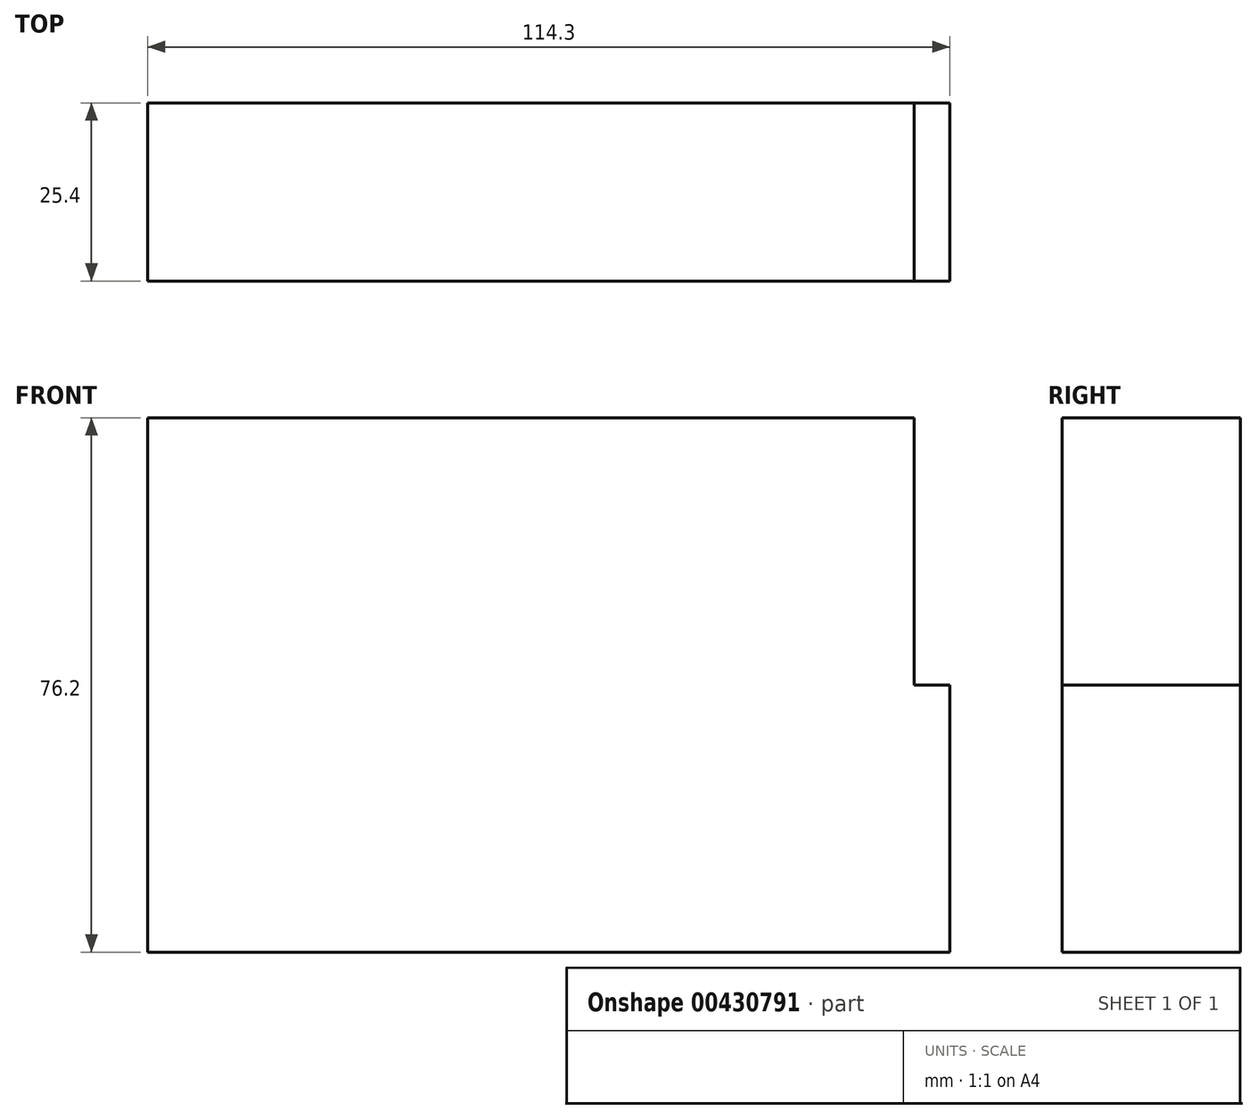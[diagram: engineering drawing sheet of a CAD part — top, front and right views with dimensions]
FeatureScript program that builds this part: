
annotation { "Feature Type Name" : "Feature", "Feature Type Description" : "" }
export const myFeature = defineFeature(function(context is Context, id is Id, definition is map)
    precondition{}
    {
        {
            var Q0;
            Q0=qCreatedBy(makeId("Front.planeOp"),FACE);
            var sketch = newSketch(context, id + "F0", { "sketchPlane" : qUnion([Q0])});
            skLineSegment(sketch, "E0.bottom", {"start": v(0, 0) * mm, "end": v(114.3, 0) * mm});
            skLineSegment(sketch, "E0.top", {"start": v(0, 76.2) * mm, "end": v(109.22, 76.2) * mm});
            skLineSegment(sketch, "E0.left", {"start": v(0, 0) * mm, "end": v(0, 76.2) * mm});
            skLineSegment(sketch, "E0.right", {"start": v(114.3, 0) * mm, "end": v(114.3, 38.1) * mm});
            skLineSegment(sketch, "E1.top", {"start": v(114.3, 38.1) * mm, "end": v(109.22, 38.1) * mm});
            skLineSegment(sketch, "E1.right", {"start": v(109.22, 76.2) * mm, "end": v(109.22, 38.1) * mm});
            skSolve(sketch);
        }
        {
            var Q0;
            Q0 = qSketchRegion(id + "F0", true);
            extrude(context, id + "F1", {"entities" : qUnion([Q0]), "depth" : 25.4 * mm});
        }
    });
